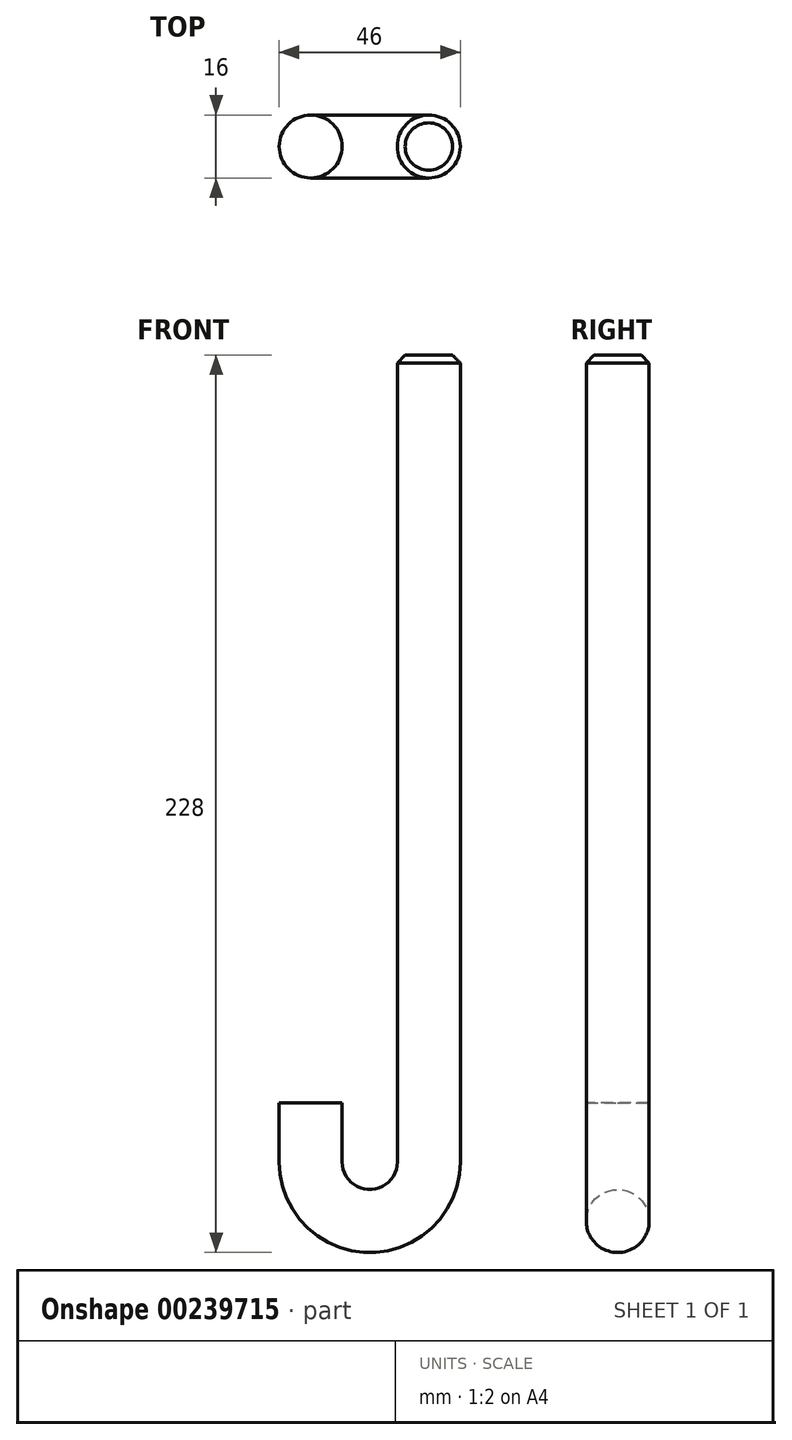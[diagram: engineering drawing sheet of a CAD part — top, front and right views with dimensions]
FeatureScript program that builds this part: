
annotation { "Feature Type Name" : "Feature", "Feature Type Description" : "" }
export const myFeature = defineFeature(function(context is Context, id is Id, definition is map)
    precondition{}
    {
        {
            var Q0;
            Q0=qCreatedBy(makeId("Top.planeOp"),FACE);
            var sketch = newSketch(context, id + "F0", { "sketchPlane" : qUnion([Q0])});
            skCircle(sketch, "E0", {"center": v(0, 0) * mm, "radius": 8 * mm});
            skSolve(sketch);
        }
        {
            var Q0;
            Q0=qCreatedBy(makeId("Front.planeOp"),FACE);
            var sketch = newSketch(context, id + "F1", { "sketchPlane" : qUnion([Q0])});
            skLineSegment(sketch, "E1", {"start": v(0, 0) * mm, "end": v(0, -205) * mm});
            skLineSegment(sketch, "E2", {"start": v(-15, -220) * mm, "end": v(-15, -220) * mm});
            skLineSegment(sketch, "E3", {"start": v(-30, -205) * mm, "end": v(-30, -190) * mm});
            skPoint(sketch, "E4.visualSharp", {"position": v(0, -220) * mm});
            skArc(sketch, "E4.filletArc", {"start": v(-15, -220) * mm, "mid": v(-4.4, -215.6) * mm, "end": v(0, -205) * mm});
            skPoint(sketch, "E5.visualSharp", {"position": v(-30, -220) * mm});
            skArc(sketch, "E5.filletArc", {"start": v(-30, -205) * mm, "mid": v(-25.6, -215.6) * mm, "end": v(-15, -220) * mm});
            skSolve(sketch);
        }
        {
            var Q0;
            Q0=makeQuery(id+"F0.imprint","IMPRINT",FACE,{"disambiguationData":[TD([[makeQuery(id+"F0.imprint","IMPRINT",EDGE,{"derivedFrom":sQuery(id+"F0.wireOp",EDGE,"E0")}),1.0]])]});
            var Q1;
            Q1 = qConstructionFilter(qBodyType(qCreatedBy(id + "F1" ,EDGE), BodyType.WIRE), ConstructionObject.NO);
            sweep(context, id + "F2", {"profiles" : qUnion([Q0]), "path" : qUnion([Q1])});
        }
        {
            var Q0;
            Q0=makeQuery(id+"F2.opSweep","CAP_EDGE",EDGE,{"disambiguationData":[OSD([sQuery(id+"F0.wireOp",EDGE,"E0"),sQuery(id+"F1.wireOp",VERTEX,"E1.start")])],"isStart":true});
            chamfer(context, id + "F3", {"entities" : qUnion([Q0]), "width" : 2 * mm, "tangentPropagation" : true});
        }
    });
